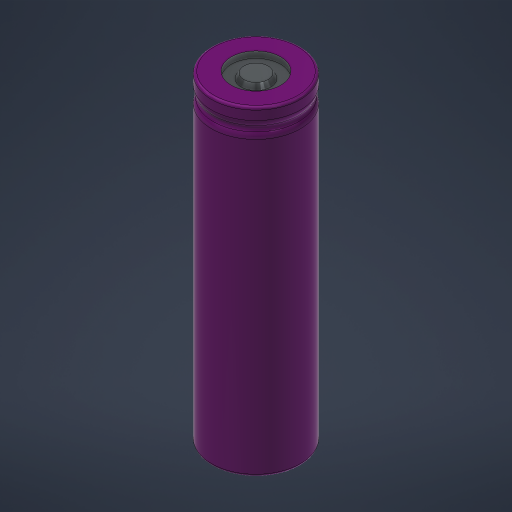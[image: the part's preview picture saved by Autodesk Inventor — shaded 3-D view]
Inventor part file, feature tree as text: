
AUTODESK INVENTOR PART (.ipt)
format: ipt  version: 2024.3 (Build 283343010, 343A)  size: 216,064 bytes
history: native  units: mm
features: revolve x1, fillet x1, sketch x1
ambient origin geometry x8: Origin, YZ Plane, XZ Plane, XY Plane, X Axis, Y Axis, Z Axis, Center Point
bodies: Body1 (feature_tree)
feature tree (3):
  revolve  "Umdrehung1"
  fillet  "Rundung1"  Radius=18.0mm
  sketch  "Skizze1"  dims[d5=1.0mm d6=19.0mm d7=0.5mm d8=0.3mm d9=14.0mm d10=1.0mm d11=10.0mm d12=6.0mm d13=4.0mm d14=60.0deg d15=90.0deg d16=2.0mm d17=0.3mm d18=65.0mm]
